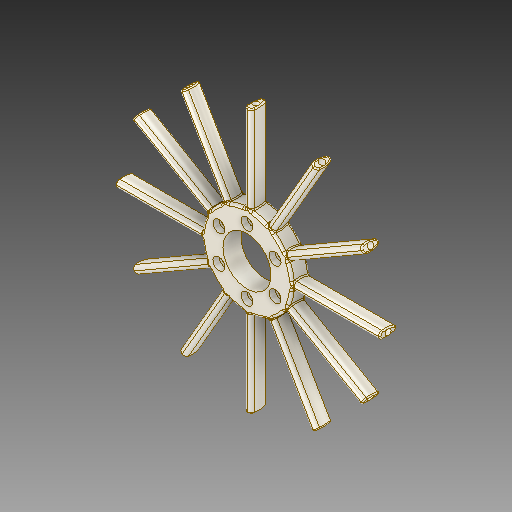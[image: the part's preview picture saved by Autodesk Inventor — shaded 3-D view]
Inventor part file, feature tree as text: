
AUTODESK INVENTOR PART (.ipt)
format: ipt  version: 2019 (Build 230136000, 136)  size: 2,203,648 bytes
history: native  units: mm
features: fillet x5, extrude x3, sketch x2, hole x2, pattern_circular x2, plane x1
ambient origin geometry x8: Origin, YZ Plane, XZ Plane, XY Plane, X Axis, Y Axis, Z Axis, Center Point
bodies: Solid1 (feature_tree)
feature tree (15):
  sketch  "Sketch1"  dims[d0=75.0mm d1=220.0mm]
  extrude  "Extrusion1"  Depth=220.0mm
  plane  "Work Plane1"
  extrude  "Extrusion2"  Depth=15.0mm TaperAngle=0.0deg
  fillet  "Fillet1"  Radius=5.0mm
  fillet  "Fillet2"  Radius=1.5mm
  fillet  "Fillet3"  Radius=20.0mm
  hole  "Hole1"  [1 undecoded]
  pattern_circular  "Circular Pattern1"  [2 undecoded]
  extrude  "Extrusion3"  Depth=2.0mm
  hole  "Hole2"  [1 undecoded]
  pattern_circular  "Circular Pattern2"  Count=23  [1 undecoded]
  fillet  "Fillet4"  Radius=120.0mm
  fillet  "Fillet6"  [1 undecoded]
  sketch  "Sketch4"  dims[d2=40.0mm d3=15.0mm d4=0.0mm d5=5.0mm d8=1.5mm d9=20.0mm d10=0.3mm d11=73.0mm d12=0.0mm d13=0.0mm d14=3.125mm d15=2.0mm d16=1.0mm d19=5.0mm d20=6.0mm d21=4.0mm d22=2.0mm d23=90.0deg d24=8.0mm d25=20.594885mm d26=230.0mm d27=120.0mm d28=360.0deg d30=0.0mm d31=0.0mm d32=2.5mm d33=0.5mm d34=0.5mm d36=27.0mm d37=5.5mm d38=6.0mm d39=10.0mm d40=5.0mm d41=90.0deg d42=8.0mm d43=20.594885mm d44=60.0mm d45=360.0deg d47=2.0mm d48=7.5mm d50=1.0mm]
note: 6 required parameter values undecoded (feature->parameter linkage not recoverable at this tier; creation-order binding heuristic only, values carry confidence <= 0.55)
